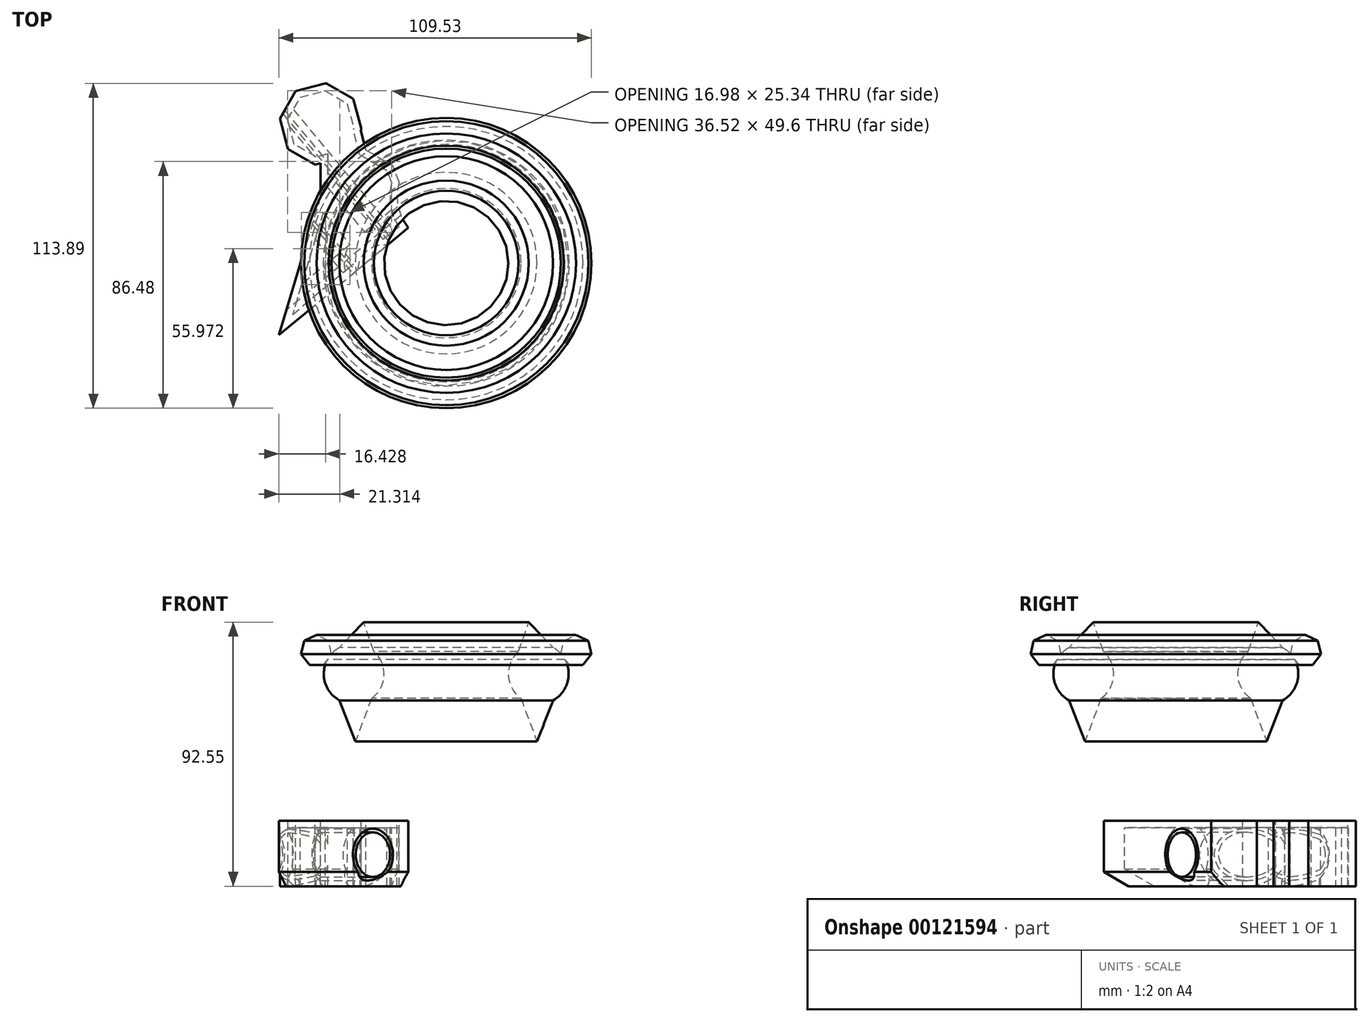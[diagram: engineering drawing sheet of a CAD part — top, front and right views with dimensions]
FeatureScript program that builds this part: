
annotation { "Feature Type Name" : "Feature", "Feature Type Description" : "" }
export const myFeature = defineFeature(function(context is Context, id is Id, definition is map)
    precondition{}
    {
        {
            var Q0;
            Q0=qCreatedBy(makeId("Top.planeOp"),FACE);
            var sketch = newSketch(context, id + "F0", { "sketchPlane" : qUnion([Q0])});
            skLineSegment(sketch, "E0", {"start": v(-44, 0) * mm, "end": v(-44, 12.08) * mm});
            skLineSegment(sketch, "E1", {"start": v(-32.46, 18.74) * mm, "end": v(-14.9, 8.6) * mm});
            skLineSegment(sketch, "E2", {"start": v(-44, 0) * mm, "end": v(-58.66, -48.64) * mm});
            skLineSegment(sketch, "E3", {"start": v(-58.66, -48.64) * mm, "end": v(-13.24, -10.98) * mm});
            skArc(sketch, "E4", {"start": v(-14.9, 8.6) * mm, "mid": v(-17.14, -1.45) * mm, "end": v(-13.24, -10.98) * mm});
            skArc(sketch, "E5.cCircle", {"start": v(-32.46, 18.74) * mm, "mid": v(-50.65, 36.93) * mm, "end": v(-44, 12.08) * mm, "construction": true});
            skLineSegment(sketch, "E5.0", {"start": v(-58.29, 27.28) * mm, "end": v(-52.77, 36.84) * mm});
            skLineSegment(sketch, "E5.1", {"start": v(-52.77, 36.84) * mm, "end": v(-42.11, 39.7) * mm});
            skLineSegment(sketch, "E5.2", {"start": v(-42.11, 39.7) * mm, "end": v(-32.56, 34.18) * mm});
            skLineSegment(sketch, "E5.3", {"start": v(-32.56, 34.18) * mm, "end": v(-29.7, 23.52) * mm});
            skLineSegment(sketch, "E5.4", {"start": v(-29.7, 23.52) * mm, "end": v(-32.46, 18.74) * mm});
            skLineSegment(sketch, "E5.5", {"start": v(-44, 11.61) * mm, "end": v(-45.88, 11.1) * mm});
            skLineSegment(sketch, "E5.6", {"start": v(-45.88, 11.1) * mm, "end": v(-55.43, 16.62) * mm});
            skLineSegment(sketch, "E5.7", {"start": v(-55.43, 16.62) * mm, "end": v(-58.29, 27.28) * mm});
            skPoint(sketch, "E5.0.midPoint", {"position": v(-55.53, 32.06) * mm});
            skPoint(sketch, "E6.orphan", {"position": v(-35.22, 13.96) * mm});
            skSolve(sketch);
        }
        {
            var Q0;
            Q0=makeQuery(id+"F0.imprint","IMPRINT",FACE,{"disambiguationData":[TD([[makeQuery(id+"F0.imprint","IMPRINT",EDGE,{"derivedFrom":sQuery(id+"F0.wireOp",EDGE,"E1")}),-1.0]])]});
            extrude(context, id + "F1", {"entities" : qUnion([Q0]), "oppositeDirection" : true, "depth" : 23 * mm});
        }
        {
            var Q0;
            Q0=makeQuery(id+"F1.opExtrude","SWEPT_FACE",FACE,{"disambiguationData":[OSD([sQuery(id+"F0.wireOp",EDGE,"E3")])]});
            var sketch = newSketch(context, id + "F2", { "sketchPlane" : qUnion([Q0])});
            skCircle(sketch, "E7", {"center": v(-33.39, -11.93) * mm, "radius": 7.8 * mm});
            skCircle(sketch, "E8", {"center": v(-33.39, -11.93) * mm, "radius": 9.07 * mm});
            skSolve(sketch);
        }
        {
            var Q0;
            Q0=makeQuery(id+"F2.imprint","IMPRINT",FACE,{"disambiguationData":[TD([[makeQuery(id+"F2.imprint","IMPRINT",EDGE,{"derivedFrom":sQuery(id+"F2.wireOp",EDGE,"E7")}),-1.0]])]});
            extrude(context, id + "F3", {"entities" : qUnion([Q0]), "operationType" : NewBodyOperationType.REMOVE, "oppositeDirection" : true, "depth" : 77.44 * mm});
        }
        {
            var Q0;
            Q0=makeQuery(id+"F1.opExtrude","SWEPT_EDGE",EDGE,{"disambiguationData":[OSD([sQuery(id+"F0.wireOp",EDGE,"E5.1"),sQuery(id+"F0.wireOp",EDGE,"E5.2")])]});
            var Q1;
            Q1=makeQuery(id+"F1.opExtrude","SWEPT_EDGE",EDGE,{"disambiguationData":[OSD([sQuery(id+"F0.wireOp",EDGE,"E5.2"),sQuery(id+"F0.wireOp",EDGE,"E5.3")])]});
            var Q2;
            Q2=makeQuery(id+"F1.opExtrude","SWEPT_EDGE",EDGE,{"disambiguationData":[OSD([sQuery(id+"F0.wireOp",EDGE,"E5.3"),sQuery(id+"F0.wireOp",EDGE,"E5.4")])]});
            fillet(context, id + "F4", {"entities" : qUnion([Q0, Q1, Q2]), "radius" : 1 * mm, "tangentPropagation" : true, "allowEdgeOverflow" : false});
        }
        {
            var Q0;
            Q0=makeQuery(id+"F1.opExtrude","SWEPT_EDGE",EDGE,{"disambiguationData":[OSD([sQuery(id+"F0.wireOp",EDGE,"E1"),sQuery(id+"F0.wireOp",EDGE,"E4")])]});
            var Q1;
            Q1=makeQuery(id+"F1.opExtrude","SWEPT_EDGE",EDGE,{"disambiguationData":[OSD([sQuery(id+"F0.wireOp",EDGE,"E1"),sQuery(id+"F0.wireOp",EDGE,"E5.4")])]});
            chamfer(context, id + "F5", {"entities" : qUnion([Q0, Q1]), "width" : 5 * mm, "tangentPropagation" : true});
        }
        {
            var Q0;
            Q0=makeQuery(id+"F1.opExtrude","CAP_EDGE",EDGE,{"disambiguationData":[OSD([sQuery(id+"F0.wireOp",EDGE,"E3")])],"isStart":false});
            chamfer(context, id + "F6", {"entities" : qUnion([Q0]), "width" : 5 * mm, "tangentPropagation" : true});
        }
        {
            var Q0;
            Q0=makeQuery(id+"F1.opExtrude","CAP_FACE",FACE,{"disambiguationData":[OSD([sQuery(id+"F0.wireOp",EDGE,"E0"),sQuery(id+"F0.wireOp",EDGE,"E1"),sQuery(id+"F0.wireOp",EDGE,"E2"),sQuery(id+"F0.wireOp",EDGE,"E3"),sQuery(id+"F0.wireOp",EDGE,"E4"),sQuery(id+"F0.wireOp",EDGE,"E5.0"),sQuery(id+"F0.wireOp",EDGE,"E5.1"),sQuery(id+"F0.wireOp",EDGE,"E5.2"),sQuery(id+"F0.wireOp",EDGE,"E5.3"),sQuery(id+"F0.wireOp",EDGE,"E5.4"),sQuery(id+"F0.wireOp",EDGE,"E5.5"),sQuery(id+"F0.wireOp",EDGE,"E5.6"),sQuery(id+"F0.wireOp",EDGE,"E5.7")])],"isStart":false});
            shell(context, id + "F7", {"entities" : qUnion([Q0]), "thickness" : 2.5 * mm});
        }
        {
            var Q0;
            Q0=qCreatedBy(makeId("Right.planeOp"),FACE);
            var sketch = newSketch(context, id + "F8", { "sketchPlane" : qUnion([Q0])});
            skArc(sketch, "E9", {"start": v(16.76, 58.5) * mm, "mid": v(15.5, 59.69) * mm, "end": v(14.04, 60.65) * mm});
            skLineSegment(sketch, "E10", {"start": v(8.94, 51.4) * mm, "end": v(-23.4, 51.4) * mm});
            skLineSegment(sketch, "E11", {"start": v(14.04, 60.65) * mm, "end": v(5.52, 69.55) * mm});
            skLineSegment(sketch, "E12", {"start": v(5.52, 69.55) * mm, "end": v(1.92, 59.29) * mm});
            skLineSegment(sketch, "E13", {"start": v(14.04, 42.16) * mm, "end": v(8.41, 27.74) * mm});
            skLineSegment(sketch, "E14", {"start": v(8.41, 27.74) * mm, "end": v(2.77, 42.83) * mm});
            skArc(sketch, "E15.cCircle", {"start": v(18.22, 56.44) * mm, "mid": v(26.92, 60.68) * mm, "end": v(17.24, 60.64) * mm, "construction": true});
            skLineSegment(sketch, "E15.0", {"start": v(19.72, 54.58) * mm, "end": v(18.22, 56.44) * mm});
            skLineSegment(sketch, "E15.1", {"start": v(16.72, 58.3) * mm, "end": v(17.76, 62.97) * mm});
            skLineSegment(sketch, "E15.2", {"start": v(17.76, 62.97) * mm, "end": v(22.06, 65.06) * mm});
            skLineSegment(sketch, "E15.3", {"start": v(22.06, 65.06) * mm, "end": v(26.38, 63.01) * mm});
            skLineSegment(sketch, "E15.4", {"start": v(26.38, 63.01) * mm, "end": v(27.46, 58.36) * mm});
            skLineSegment(sketch, "E15.5", {"start": v(27.46, 58.36) * mm, "end": v(24.5, 54.6) * mm});
            skLineSegment(sketch, "E15.6", {"start": v(24.5, 54.6) * mm, "end": v(19.72, 54.58) * mm});
            skPoint(sketch, "E15.0.midPoint", {"position": v(18.22, 56.44) * mm});
            skArc(sketch, "E16.trimOffspring", {"start": v(1.92, 59.29) * mm, "mid": v(-1.6, 50.86) * mm, "end": v(2.77, 42.83) * mm});
            skArc(sketch, "E17.trimOffspring", {"start": v(14.04, 42.16) * mm, "mid": v(19.07, 48.44) * mm, "end": v(18.22, 56.44) * mm});
            skLineSegment(sketch, "E18", {"start": v(-23.4, 51.4) * mm, "end": v(-23.4, 48.4) * mm});
            skSolve(sketch);
        }
        {
            var Q0;
            {var subQ1=sQuery(id+"F8.wireOp",EDGE,"E9");Q0=makeQuery(id+"F8.imprint","IMPRINT",FACE,{"disambiguationData":[TD([[makeQuery(id+"F8.imprint","IMPRINT",EDGE,{"derivedFrom":subQ1}),1.0]])]});}
            var Q1;
            Q1=sQuery(id+"F8.wireOp",EDGE,"E18");
            revolve(context, id + "F9", {"operationType" : NewBodyOperationType.ADD, "entities" : qUnion([Q0]), "axis" : qUnion([Q1]), "revolveType" : RevolveType.FULL});
        }
    });
